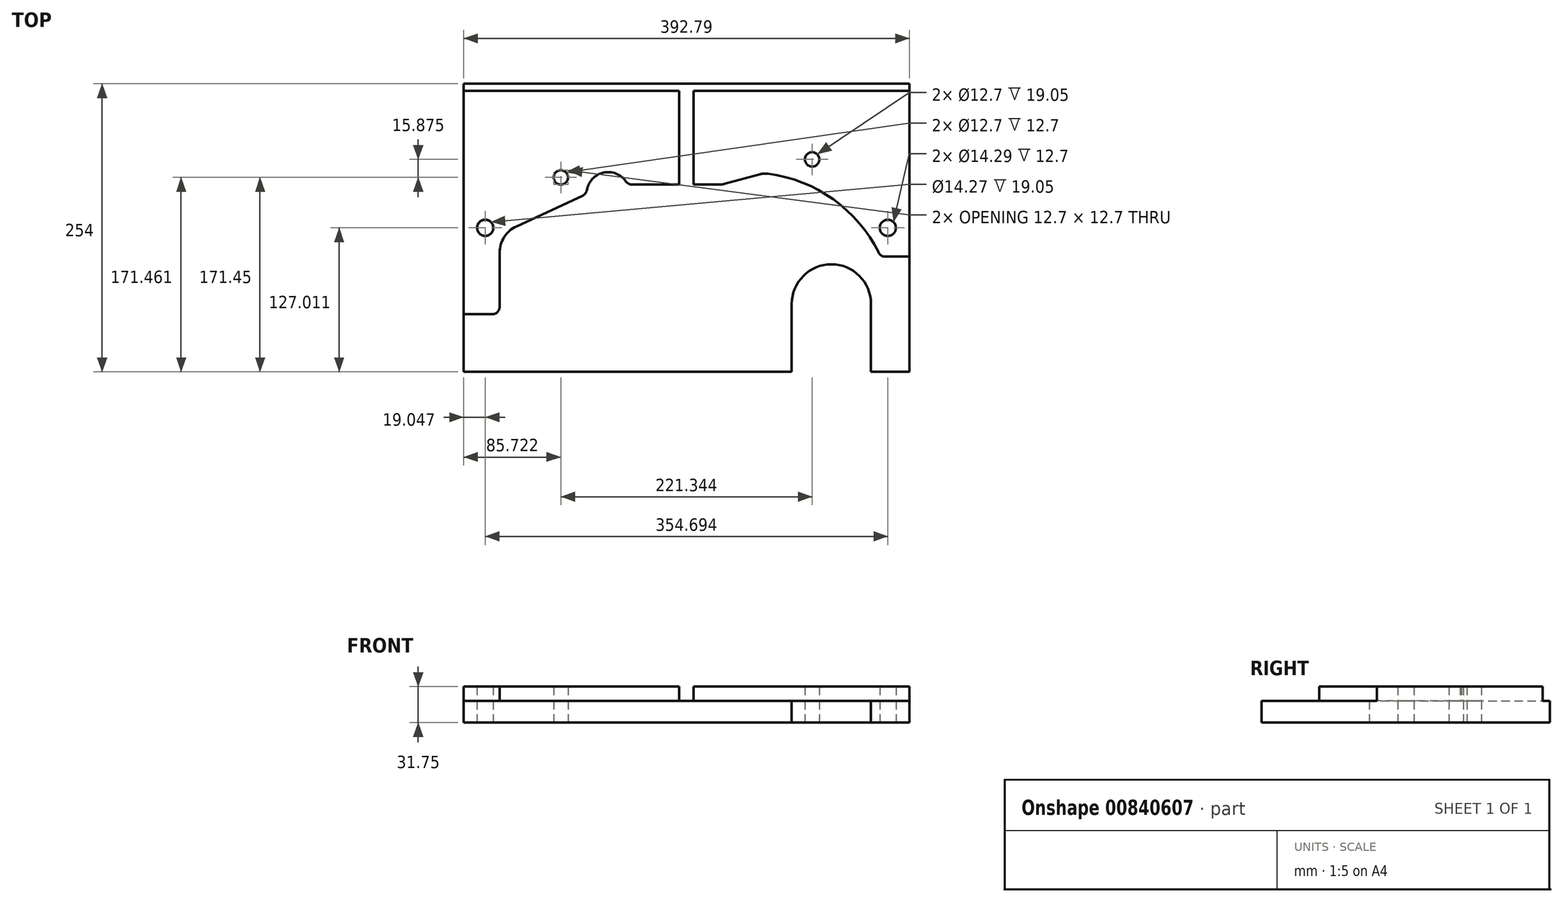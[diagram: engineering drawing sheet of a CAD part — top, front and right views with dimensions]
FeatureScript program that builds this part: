
annotation { "Feature Type Name" : "Feature", "Feature Type Description" : "" }
export const myFeature = defineFeature(function(context is Context, id is Id, definition is map)
    precondition{}
    {
        {
            var Q0;
            Q0=qCreatedBy(makeId("Top.planeOp"),FACE);
            var sketch = newSketch(context, id + "F0", { "sketchPlane" : qUnion([Q0])});
            skLineSegment(sketch, "E0", {"start": v(153.35, -127) * mm, "end": v(-112.4, -127) * mm});
            skArc(sketch, "E1", {"start": v(-112.4, -127) * mm, "mid": v(-149.75, -68.16) * mm, "end": v(-187.1, -127) * mm});
            skLineSegment(sketch, "E2", {"start": v(-187.1, -127) * mm, "end": v(-239.44, -127) * mm});
            skLineSegment(sketch, "E3", {"start": v(-239.44, -127) * mm, "end": v(-239.44, 127) * mm});
            skLineSegment(sketch, "E4", {"start": v(-239.44, 127) * mm, "end": v(153.35, 127) * mm});
            skLineSegment(sketch, "E5", {"start": v(153.35, 127) * mm, "end": v(153.35, -127) * mm});
            skCircle(sketch, "E6", {"center": v(-153.72, 44.45) * mm, "radius": 6.35 * mm});
            skCircle(sketch, "E7", {"center": v(67.63, 60.33) * mm, "radius": 6.35 * mm});
            skCircle(sketch, "E8", {"center": v(-220.4, 0) * mm, "radius": 7.14 * mm});
            skCircle(sketch, "E9", {"center": v(134.3, 0) * mm, "radius": 7.14 * mm});
            skCircle(sketch, "E10", {"center": v(84.58, -67.07) * mm, "radius": 34.93 * mm});
            skSolve(sketch);
        }
        {
            var Q0;
            Q0=qSketchRegion(id+"F0",true);
            extrude(context, id + "F1", {"entities" : qUnion([Q0]), "depth" : 19.05 * mm, "offsetDistance" : 25.4 * mm});
        }
        {
            var Q0;
            Q0=makeQuery(id+"F1.opExtrude","CAP_FACE",FACE,{"disambiguationData":[OSD([sQuery(id+"F0.wireOp",EDGE,"E0"),sQuery(id+"F0.wireOp",EDGE,"E1"),sQuery(id+"F0.wireOp",EDGE,"E2"),sQuery(id+"F0.wireOp",EDGE,"E3"),sQuery(id+"F0.wireOp",EDGE,"E4"),sQuery(id+"F0.wireOp",EDGE,"E5"),sQuery(id+"F0.wireOp",EDGE,"E8"),sQuery(id+"F0.wireOp",EDGE,"E10"),sQuery(id+"F0.wireOp",EDGE,"E9"),sQuery(id+"F0.wireOp",EDGE,"E6"),sQuery(id+"F0.wireOp",EDGE,"E7")])],"isStart":false});
            var sketch = newSketch(context, id + "F2", { "sketchPlane" : qUnion([Q0])});
            skArc(sketch, "E11", {"start": v(-193.03, 1.2) * mm, "mid": v(-203.71, -8.17) * mm, "end": v(-207.7, -21.82) * mm});
            skArc(sketch, "E12", {"start": v(28.82, 47.68) * mm, "mid": v(25.06, 47.8) * mm, "end": v(21.36, 47.17) * mm});
            skLineSegment(sketch, "E13", {"start": v(-9.42, 38.78) * mm, "end": v(21.36, 47.17) * mm});
            skArc(sketch, "E14", {"start": v(-14.43, 38.11) * mm, "mid": v(-11.9, 38.28) * mm, "end": v(-9.42, 38.78) * mm});
            skLineSegment(sketch, "E15", {"start": v(21.36, 47.17) * mm, "end": v(-9.42, 38.78) * mm});
            skArc(sketch, "E16", {"start": v(126.32, -21.97) * mm, "mid": v(86.3, 25.08) * mm, "end": v(28.82, 47.68) * mm});
            skCircle(sketch, "E17", {"center": v(-153.72, 44.46) * mm, "radius": 6.35 * mm});
            skCircle(sketch, "E18", {"center": v(67.63, 60.34) * mm, "radius": 6.35 * mm});
            skCircle(sketch, "E19", {"center": v(-220.4, 0.01) * mm, "radius": 7.14 * mm});
            skCircle(sketch, "E20", {"center": v(134.3, 0.01) * mm, "radius": 7.14 * mm});
            skLineSegment(sketch, "E21", {"start": v(-239.44, 120.66) * mm, "end": v(-49.4, 120.66) * mm});
            skLineSegment(sketch, "E22", {"start": v(-49.4, 120.66) * mm, "end": v(-239.44, 120.66) * mm});
            skLineSegment(sketch, "E23", {"start": v(-49.4, 120.66) * mm, "end": v(-49.4, 38.11) * mm});
            skLineSegment(sketch, "E24", {"start": v(-49.4, 38.11) * mm, "end": v(-49.4, 120.66) * mm});
            skLineSegment(sketch, "E25", {"start": v(-36.7, 38.11) * mm, "end": v(-36.7, 120.66) * mm});
            skLineSegment(sketch, "E26", {"start": v(-36.7, 120.66) * mm, "end": v(-36.7, 38.11) * mm});
            skLineSegment(sketch, "E27", {"start": v(-36.7, 120.66) * mm, "end": v(153.35, 120.66) * mm});
            skLineSegment(sketch, "E28", {"start": v(153.35, 120.66) * mm, "end": v(-36.7, 120.66) * mm});
            skLineSegment(sketch, "E29", {"start": v(-49.4, 38.11) * mm, "end": v(-91.17, 38.11) * mm});
            skLineSegment(sketch, "E30", {"start": v(-91.17, 38.11) * mm, "end": v(-49.4, 38.11) * mm});
            skLineSegment(sketch, "E31", {"start": v(-239.44, -76.19) * mm, "end": v(-239.44, 120.66) * mm});
            skLineSegment(sketch, "E32", {"start": v(-214.04, -76.19) * mm, "end": v(-239.44, -76.19) * mm});
            skArc(sketch, "E33", {"start": v(-214.04, -76.19) * mm, "mid": v(-209.55, -74.33) * mm, "end": v(-207.7, -69.84) * mm});
            skLineSegment(sketch, "E34", {"start": v(-207.7, -21.82) * mm, "end": v(-207.7, -69.84) * mm});
            skArc(sketch, "E35", {"start": v(-193.03, 1.2) * mm, "mid": v(-203.72, -8.17) * mm, "end": v(-207.7, -21.82) * mm});
            skLineSegment(sketch, "E36", {"start": v(-134.46, 28.51) * mm, "end": v(-193.03, 1.2) * mm});
            skArc(sketch, "E37", {"start": v(-134.46, 28.51) * mm, "mid": v(-132.09, 30.42) * mm, "end": v(-130.88, 33.22) * mm});
            skArc(sketch, "E38", {"start": v(-96.4, 40.86) * mm, "mid": v(-116.21, 48.66) * mm, "end": v(-130.88, 33.22) * mm});
            skArc(sketch, "E39", {"start": v(-96.4, 40.86) * mm, "mid": v(-94.12, 38.84) * mm, "end": v(-91.17, 38.11) * mm});
            skLineSegment(sketch, "E40", {"start": v(-239.44, -76.19) * mm, "end": v(-214.04, -76.19) * mm});
            skLineSegment(sketch, "E41", {"start": v(131.96, -25.39) * mm, "end": v(153.35, -25.39) * mm});
            skArc(sketch, "E42", {"start": v(126.27, -21.86) * mm, "mid": v(128.6, -24.44) * mm, "end": v(131.96, -25.39) * mm});
            skArc(sketch, "E43", {"start": v(126.27, -21.86) * mm, "mid": v(86.25, 25.12) * mm, "end": v(28.82, 47.68) * mm});
            skLineSegment(sketch, "E44", {"start": v(-36.7, 38.11) * mm, "end": v(-14.43, 38.11) * mm});
            skLineSegment(sketch, "E45", {"start": v(-193.03, 1.2) * mm, "end": v(-134.46, 28.51) * mm});
            skLineSegment(sketch, "E46", {"start": v(-207.7, -69.84) * mm, "end": v(-207.7, -21.82) * mm});
            skLineSegment(sketch, "E47", {"start": v(-239.44, 120.66) * mm, "end": v(-239.44, -76.19) * mm});
            skLineSegment(sketch, "E48", {"start": v(153.35, -25.39) * mm, "end": v(153.35, 120.66) * mm});
            skLineSegment(sketch, "E49", {"start": v(-14.43, 38.11) * mm, "end": v(-36.7, 38.11) * mm});
            skLineSegment(sketch, "E50", {"start": v(153.35, -25.39) * mm, "end": v(131.96, -25.39) * mm});
            skLineSegment(sketch, "E51", {"start": v(153.35, 120.66) * mm, "end": v(153.35, -25.39) * mm});
            skSolve(sketch);
        }
        {
            var Q0;
            Q0=qSketchRegion(id+"F2",true);
            extrude(context, id + "F3", {"entities" : qUnion([Q0]), "operationType" : NewBodyOperationType.ADD, "depth" : 12.7 * mm, "offsetDistance" : 25.4 * mm});
        }
        {
            var Q0;
            {var subQ0=sQuery(id+"F0.wireOp",EDGE,"E2");var subQ1=sQuery(id+"F0.wireOp",EDGE,"E1");var subQ2=sQuery(id+"F0.wireOp",EDGE,"E3");var subQ3=sQuery(id+"F0.wireOp",EDGE,"E0");var subQ4=sQuery(id+"F0.wireOp",EDGE,"E4");var subQ5=sQuery(id+"F0.wireOp",EDGE,"E5");var subQ6=sQuery(id+"F0.wireOp",EDGE,"E10");Q0=makeQuery(id+"F3.boolean.opBoolean","SPLIT",FACE,{"disambiguationData":[TD([makeQuery(id+"F1.opExtrude","SWEPT_FACE",FACE,{"disambiguationData":[OSD([subQ3])]})])],"derivedFrom":makeQuery(id+"F1.opExtrude","CAP_FACE",FACE,{"disambiguationData":[OSD([subQ3,subQ1,subQ0,subQ2,subQ4,subQ5,sQuery(id+"F0.wireOp",EDGE,"E8"),subQ6,sQuery(id+"F0.wireOp",EDGE,"E9"),sQuery(id+"F0.wireOp",EDGE,"E6"),sQuery(id+"F0.wireOp",EDGE,"E7")])],"isStart":false})});}
            var sketch = newSketch(context, id + "F4", { "sketchPlane" : qUnion([Q0])});
            skCircle(sketch, "E52", {"center": v(84.58, -67.07) * mm, "radius": 34.93 * mm});
            skLineSegment(sketch, "E53", {"start": v(119.5, -127) * mm, "end": v(119.5, -67.07) * mm});
            skLineSegment(sketch, "E54", {"start": v(49.65, -127) * mm, "end": v(49.65, -67.07) * mm});
            skLineSegment(sketch, "E55", {"start": v(49.65, -127) * mm, "end": v(119.5, -127) * mm});
            skSolve(sketch);
        }
        {
            var Q0;
            Q0=qSketchRegion(id+"F4",true);
            extrude(context, id + "F5", {"entities" : qUnion([Q0]), "operationType" : NewBodyOperationType.REMOVE, "oppositeDirection" : true, "depth" : 25.4 * mm, "offsetDistance" : 25.4 * mm});
        }
        {
            var Q0;
            {var subQ0=sQuery(id+"F0.wireOp",EDGE,"E2");var subQ1=sQuery(id+"F0.wireOp",EDGE,"E1");var subQ2=sQuery(id+"F0.wireOp",EDGE,"E3");var subQ3=sQuery(id+"F0.wireOp",EDGE,"E0");var subQ4=sQuery(id+"F0.wireOp",EDGE,"E4");var subQ5=sQuery(id+"F0.wireOp",EDGE,"E5");var subQ6=sQuery(id+"F0.wireOp",EDGE,"E10");Q0=makeQuery(id+"F3.boolean.opBoolean","SPLIT",FACE,{"disambiguationData":[TD([makeQuery(id+"F1.opExtrude","SWEPT_FACE",FACE,{"disambiguationData":[OSD([subQ3])]})])],"derivedFrom":makeQuery(id+"F1.opExtrude","CAP_FACE",FACE,{"disambiguationData":[OSD([subQ3,subQ1,subQ0,subQ2,subQ4,subQ5,sQuery(id+"F0.wireOp",EDGE,"E8"),subQ6,sQuery(id+"F0.wireOp",EDGE,"E9"),sQuery(id+"F0.wireOp",EDGE,"E6"),sQuery(id+"F0.wireOp",EDGE,"E7")])],"isStart":false})});}
            var sketch = newSketch(context, id + "F6", { "sketchPlane" : qUnion([Q0])});
            skArc(sketch, "E56", {"start": v(-108.47, -109.44) * mm, "mid": v(-149.75, -68.16) * mm, "end": v(-191.02, -109.44) * mm});
            skLineSegment(sketch, "E57", {"start": v(-108.47, -127) * mm, "end": v(-108.47, -109.44) * mm});
            skLineSegment(sketch, "E58", {"start": v(-191.02, -127) * mm, "end": v(-191.02, -109.44) * mm});
            skLineSegment(sketch, "E59", {"start": v(-191.02, -127) * mm, "end": v(-108.47, -127) * mm});
            skSolve(sketch);
        }
        {
            var Q0;
            Q0=qSketchRegion(id+"F6",true);
            extrude(context, id + "F7", {"entities" : qUnion([Q0]), "operationType" : NewBodyOperationType.REMOVE, "oppositeDirection" : true, "depth" : 25.4 * mm, "offsetDistance" : 25.4 * mm});
        }
        {
            var Q0;
            {var subQ0=sQuery(id+"F0.wireOp",EDGE,"E2");var subQ1=sQuery(id+"F0.wireOp",EDGE,"E1");var subQ2=sQuery(id+"F0.wireOp",EDGE,"E3");var subQ3=sQuery(id+"F0.wireOp",EDGE,"E0");var subQ4=sQuery(id+"F0.wireOp",EDGE,"E4");var subQ5=sQuery(id+"F0.wireOp",EDGE,"E5");var subQ6=sQuery(id+"F0.wireOp",EDGE,"E10");Q0=makeQuery(id+"F3.boolean.opBoolean","SPLIT",FACE,{"disambiguationData":[TD([makeQuery(id+"F1.opExtrude","SWEPT_FACE",FACE,{"disambiguationData":[OSD([subQ3])]})])],"derivedFrom":makeQuery(id+"F1.opExtrude","CAP_FACE",FACE,{"disambiguationData":[OSD([subQ3,subQ1,subQ0,subQ2,subQ4,subQ5,sQuery(id+"F0.wireOp",EDGE,"E8"),subQ6,sQuery(id+"F0.wireOp",EDGE,"E9"),sQuery(id+"F0.wireOp",EDGE,"E6"),sQuery(id+"F0.wireOp",EDGE,"E7")])],"isStart":false})});}
            var sketch = newSketch(context, id + "F8", { "sketchPlane" : qUnion([Q0])});
            skArc(sketch, "E60.0", {"start": v(-108.47, -109.44) * mm, "mid": v(-149.75, -68.16) * mm, "end": v(-191.02, -109.44) * mm});
            skPoint(sketch, "E61.0", {"position": v(-191.02, -118.22) * mm});
            skLineSegment(sketch, "E62.0", {"start": v(-191.02, -127) * mm, "end": v(-191.02, -109.44) * mm});
            skLineSegment(sketch, "E63.0", {"start": v(-108.47, -127) * mm, "end": v(-108.47, -109.44) * mm});
            skLineSegment(sketch, "E64", {"start": v(-191.02, -127) * mm, "end": v(-108.47, -127) * mm});
            skSolve(sketch);
        }
        {
            var Q0;
            Q0=qSketchRegion(id+"F8",true);
            extrude(context, id + "F9", {"entities" : qUnion([Q0]), "operationType" : NewBodyOperationType.ADD, "oppositeDirection" : true, "depth" : 19.05 * mm, "offsetDistance" : 25.4 * mm});
        }
    });
